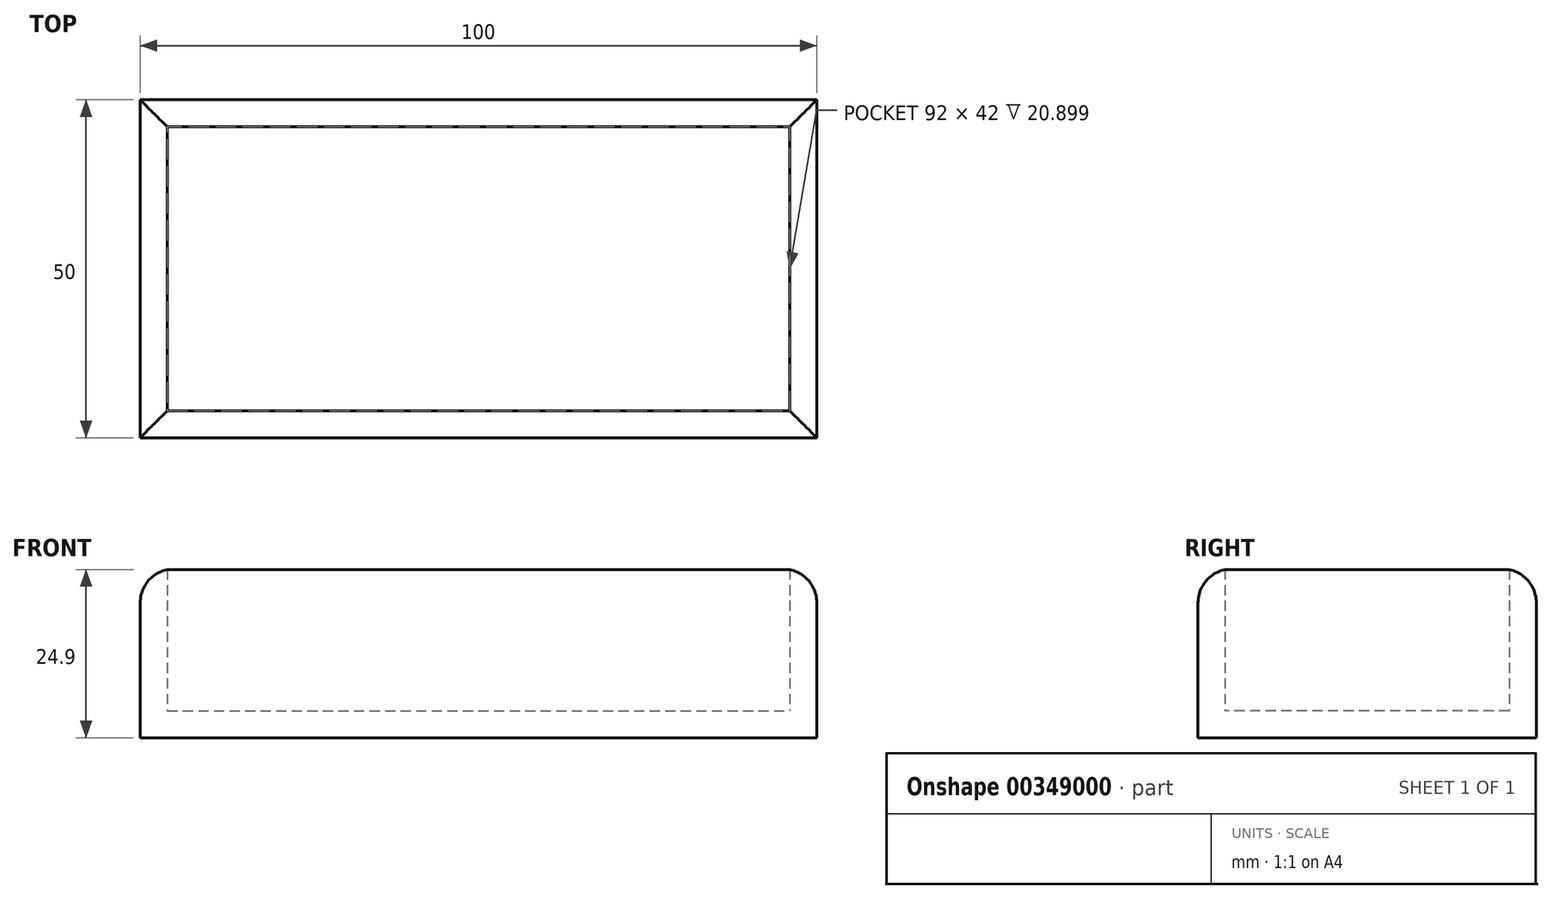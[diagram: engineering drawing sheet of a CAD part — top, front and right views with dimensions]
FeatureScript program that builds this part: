
annotation { "Feature Type Name" : "Feature", "Feature Type Description" : "" }
export const myFeature = defineFeature(function(context is Context, id is Id, definition is map)
    precondition{}
    {
        {
            var Q0;
            Q0=qCreatedBy(makeId("Top.planeOp"),FACE);
            var sketch = newSketch(context, id + "F0", { "sketchPlane" : qUnion([Q0])});
            skLineSegment(sketch, "E0.bottom", {"start": v(-54.75, 13.08) * mm, "end": v(45.25, 13.08) * mm});
            skLineSegment(sketch, "E0.top", {"start": v(-54.75, -36.92) * mm, "end": v(45.25, -36.92) * mm});
            skLineSegment(sketch, "E0.left", {"start": v(-54.75, 13.08) * mm, "end": v(-54.75, -36.92) * mm});
            skLineSegment(sketch, "E0.right", {"start": v(45.25, 13.08) * mm, "end": v(45.25, -36.92) * mm});
            skSolve(sketch);
        }
        {
            var Q0;
            Q0=makeQuery(id+"F0.imprint","IMPRINT",FACE,{"disambiguationData":[TD([[makeQuery(id+"F0.imprint","IMPRINT",EDGE,{"derivedFrom":sQuery(id+"F0.wireOp",EDGE,"E0.bottom")}),-1.0]])]});
            extrude(context, id + "F1", {"entities" : qUnion([Q0]), "depth" : 25 * mm});
        }
        {
            var Q0;
            Q0=makeQuery(id+"F1.opExtrude","CAP_FACE",FACE,{"disambiguationData":[OSD([sQuery(id+"F0.wireOp",EDGE,"E0.bottom"),sQuery(id+"F0.wireOp",EDGE,"E0.top"),sQuery(id+"F0.wireOp",EDGE,"E0.left"),sQuery(id+"F0.wireOp",EDGE,"E0.right")])],"isStart":false});
            shell(context, id + "F2", {"entities" : qUnion([Q0]), "thickness" : 4 * mm});
        }
        {
            var Q0;
            Q0=makeQuery(id+"F1.opExtrude","CAP_EDGE",EDGE,{"disambiguationData":[OSD([sQuery(id+"F0.wireOp",EDGE,"E0.left")])],"isStart":false});
            var Q1;
            Q1=makeQuery(id+"F1.opExtrude","CAP_EDGE",EDGE,{"disambiguationData":[OSD([sQuery(id+"F0.wireOp",EDGE,"E0.bottom")])],"isStart":false});
            var Q2;
            Q2=makeQuery(id+"F1.opExtrude","CAP_EDGE",EDGE,{"disambiguationData":[OSD([sQuery(id+"F0.wireOp",EDGE,"E0.right")])],"isStart":false});
            var Q3;
            Q3=makeQuery(id+"F1.opExtrude","CAP_EDGE",EDGE,{"disambiguationData":[OSD([sQuery(id+"F0.wireOp",EDGE,"E0.top")])],"isStart":false});
            fillet(context, id + "F3", {"entities" : qUnion([Q0, Q1, Q2, Q3]), "radius" : 5 * mm, "tangentPropagation" : true, "allowEdgeOverflow" : false});
        }
    });
